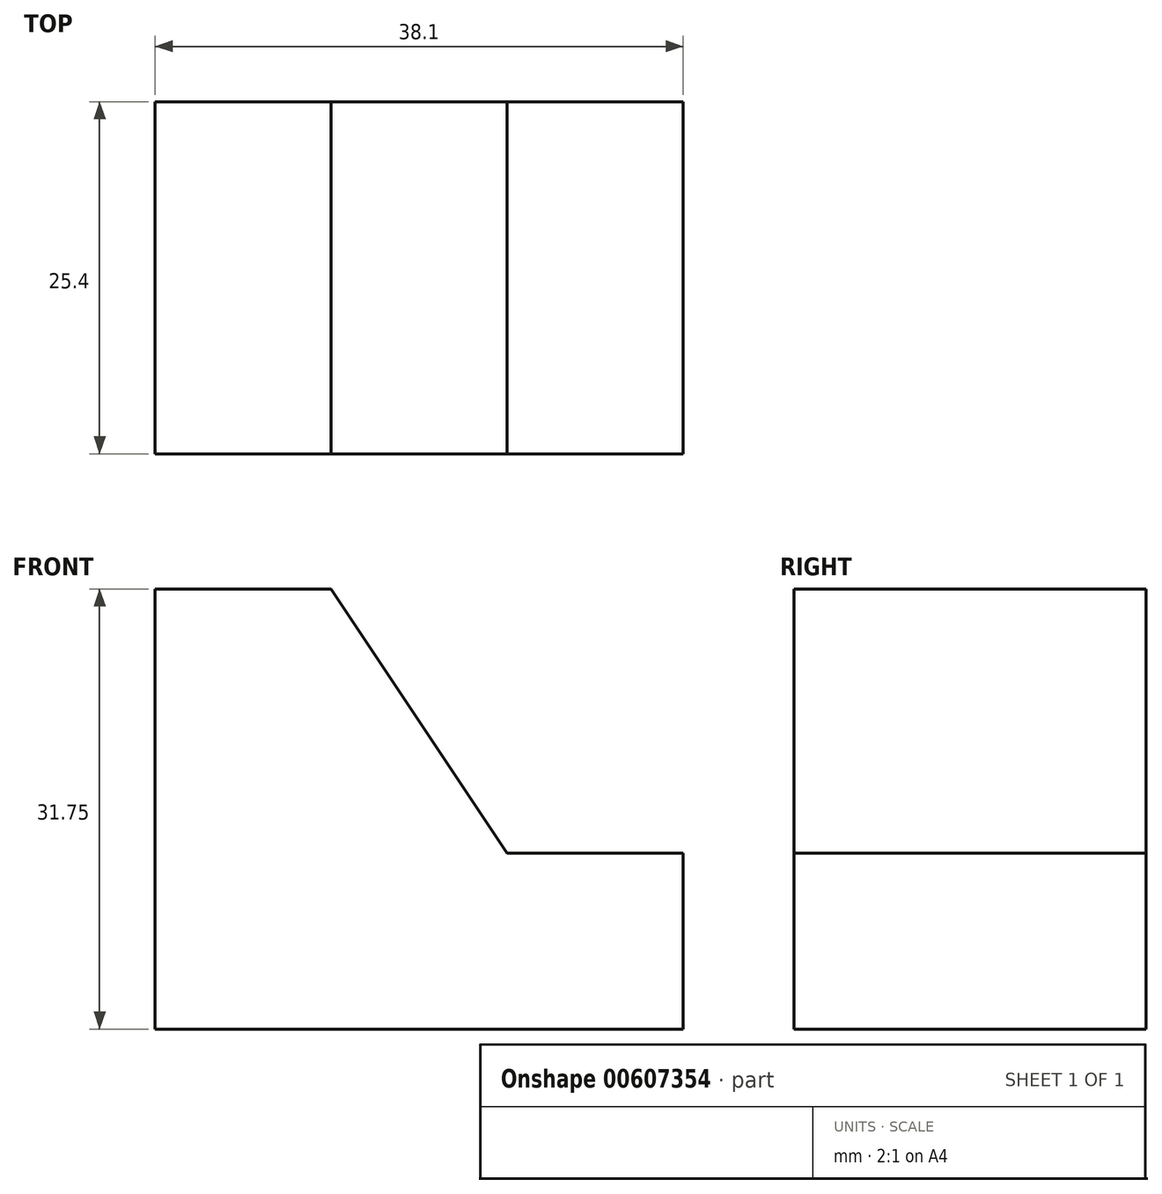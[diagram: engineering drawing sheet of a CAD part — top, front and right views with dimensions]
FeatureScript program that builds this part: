
annotation { "Feature Type Name" : "Feature", "Feature Type Description" : "" }
export const myFeature = defineFeature(function(context is Context, id is Id, definition is map)
    precondition{}
    {
        {
            var Q0;
            Q0=qCreatedBy(makeId("Front.planeOp"),FACE);
            var sketch = newSketch(context, id + "F0", { "sketchPlane" : qUnion([Q0])});
            skLineSegment(sketch, "E0", {"start": v(-17.66, 0) * mm, "end": v(20.44, 0) * mm});
            skLineSegment(sketch, "E1", {"start": v(-17.66, 0) * mm, "end": v(-17.66, 31.75) * mm});
            skLineSegment(sketch, "E2", {"start": v(-17.66, 31.75) * mm, "end": v(-4.96, 31.75) * mm});
            skLineSegment(sketch, "E3", {"start": v(20.44, 0) * mm, "end": v(20.44, 12.7) * mm});
            skLineSegment(sketch, "E4", {"start": v(20.44, 12.7) * mm, "end": v(7.74, 12.7) * mm});
            skLineSegment(sketch, "E5", {"start": v(-4.96, 31.75) * mm, "end": v(7.74, 12.7) * mm});
            skSolve(sketch);
        }
        {
            var Q0;
            Q0=makeQuery(id+"F0.imprint","IMPRINT",FACE,{"disambiguationData":[TD([[makeQuery(id+"F0.imprint","IMPRINT",EDGE,{"derivedFrom":sQuery(id+"F0.wireOp",EDGE,"E0")}),1.0]])]});
            extrude(context, id + "F1", {"entities" : qUnion([Q0]), "depth" : 25.4 * mm, "offsetDistance" : 25.4 * mm});
        }
    });
